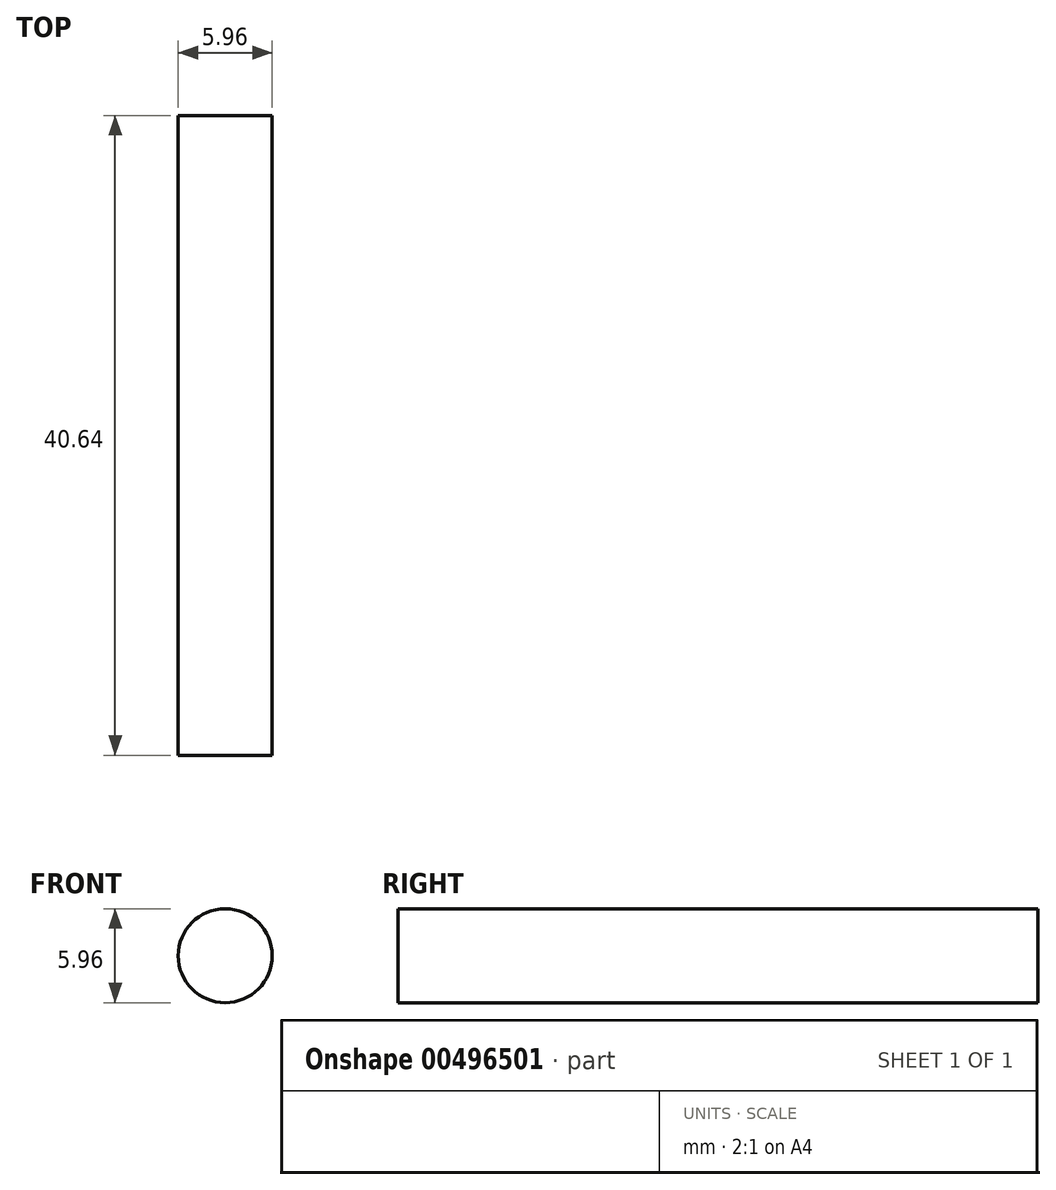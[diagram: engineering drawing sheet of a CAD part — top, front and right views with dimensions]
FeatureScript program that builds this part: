
annotation { "Feature Type Name" : "Feature", "Feature Type Description" : "" }
export const myFeature = defineFeature(function(context is Context, id is Id, definition is map)
    precondition{}
    {
        {
            var Q0;
            Q0=qCreatedBy(makeId("Front.planeOp"),FACE);
            var sketch = newSketch(context, id + "F0", { "sketchPlane" : qUnion([Q0])});
            skCircle(sketch, "E0", {"center": v(0, 0) * mm, "radius": 2.98 * mm});
            skSolve(sketch);
        }
        {
            var Q0;
            Q0=makeQuery(id+"F0.imprint","IMPRINT",FACE,{"disambiguationData":[TD([[makeQuery(id+"F0.imprint","IMPRINT",EDGE,{"derivedFrom":sQuery(id+"F0.wireOp",EDGE,"E0")}),1.0]])]});
            extrude(context, id + "F1", {"entities" : qUnion([Q0]), "endBound" : BoundingType.SYMMETRIC, "depth" : 40.64 * mm});
        }
    });
